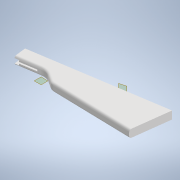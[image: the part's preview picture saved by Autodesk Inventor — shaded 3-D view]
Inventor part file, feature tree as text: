
AUTODESK INVENTOR PART (.ipt)
format: ipt  version: 2022 (Build 260153000, 153)  size: 2,971,648 bytes
history: native  units: mm
features: other x3, sketch x2, extrude x2, fillet x1
ambient origin geometry x8: Origin, YZ Plane, XZ Plane, XY Plane, X Axis, Y Axis, Z Axis, Center Point
bodies: Body1 (feature_tree)
feature tree (8):
  other  "РабПлоскость1"
  sketch  "Эскиз1"
  other  "РабПлоскость2"
  sketch  "Эскиз2"
  extrude  "Выдавливание2"  Depth=25.0mm TaperAngle=0.0deg
  extrude  "Выдавливание3"  TaperAngle=0.0deg  [1 undecoded]
  fillet  "Сопряжение1"  Radius=7.0mm
  other  "Картинка1"
note: 1 required parameter value undecoded (feature->parameter linkage not recoverable at this tier; creation-order binding heuristic only, values carry confidence <= 0.55)
